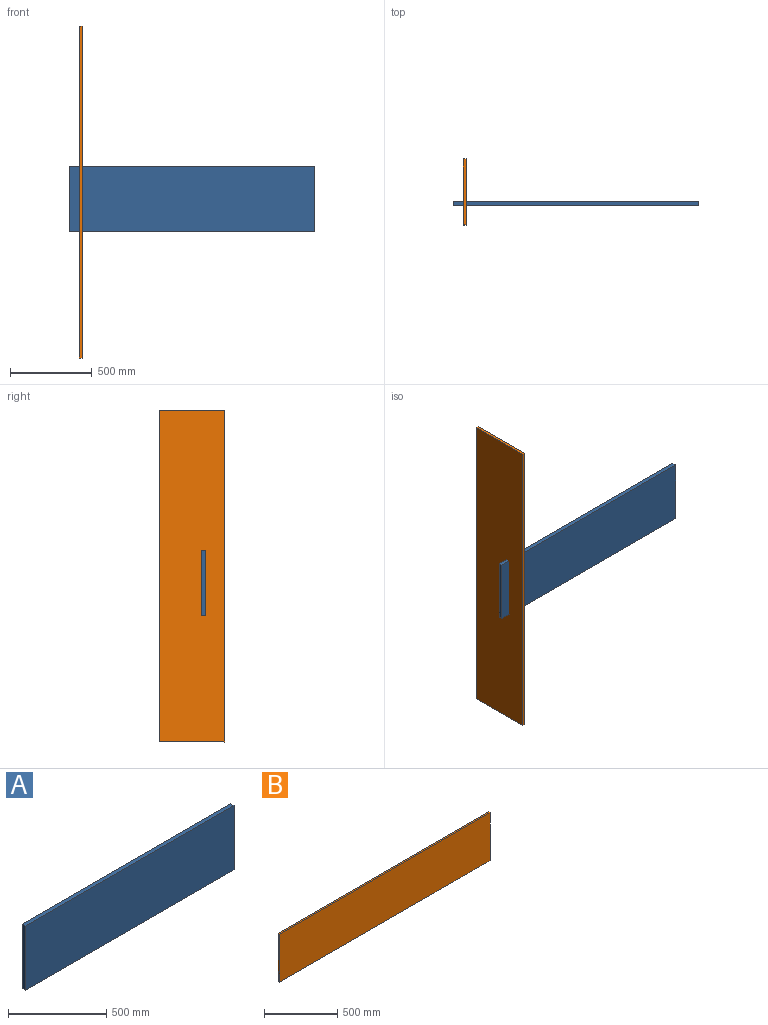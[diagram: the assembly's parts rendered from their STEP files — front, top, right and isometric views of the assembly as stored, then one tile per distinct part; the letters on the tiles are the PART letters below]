
ASSEMBLY  parts=2 mates=1
PART A: 6 faces, bbox 1500x25x400 mm
  f0: plane 1500x25mm, normal (0,0,1), area 37500mm2, adj f1,f3,f4,f5
  f1: plane 400x25mm, normal (-1,0,0), area 10000mm2, adj f0,f2,f4,f5
  f2: plane 1500x25mm, normal (0,0,-1), area 37500mm2, adj f1,f3,f4,f5
  f3: plane 400x25mm, normal (1,0,0), area 10000mm2, adj f0,f2,f4,f5
  f4: plane 1500x400mm, normal (0,-1,0), area 600000mm2, adj f0,f1,f2,f3
  f5: plane 1500x400mm, normal (0,1,0), area 600000mm2, adj f0,f1,f2,f3
PART B: 6 faces, bbox 2026x16x400 mm
  f0: plane 2026x16mm, normal (0,0,1), area 32416mm2, adj f1,f3,f4,f5
  f1: plane 400x16mm, normal (-1,0,0), area 6400mm2, adj f0,f2,f4,f5
  f2: plane 2026x16mm, normal (0,0,-1), area 32416mm2, adj f1,f3,f4,f5
  f3: plane 400x16mm, normal (1,0,0), area 6400mm2, adj f0,f2,f4,f5
  f4: plane 2026x400mm, normal (0,-1,0), area 810400mm2, adj f0,f1,f2,f3
  f5: plane 2026x400mm, normal (0,1,0), area 810400mm2, adj f0,f1,f2,f3
PLACE A t=(-257.41,328.65,-152.36)mm fixed
PLACE B rot(axis=(-0.58,-0.58,-0.58),120deg) t=(-178.41,188.36,-923.98)mm
MATE parallel A.f3 <-> B.f5  axis (1,0,0) through (1242.59,316.15,47.64)mm
